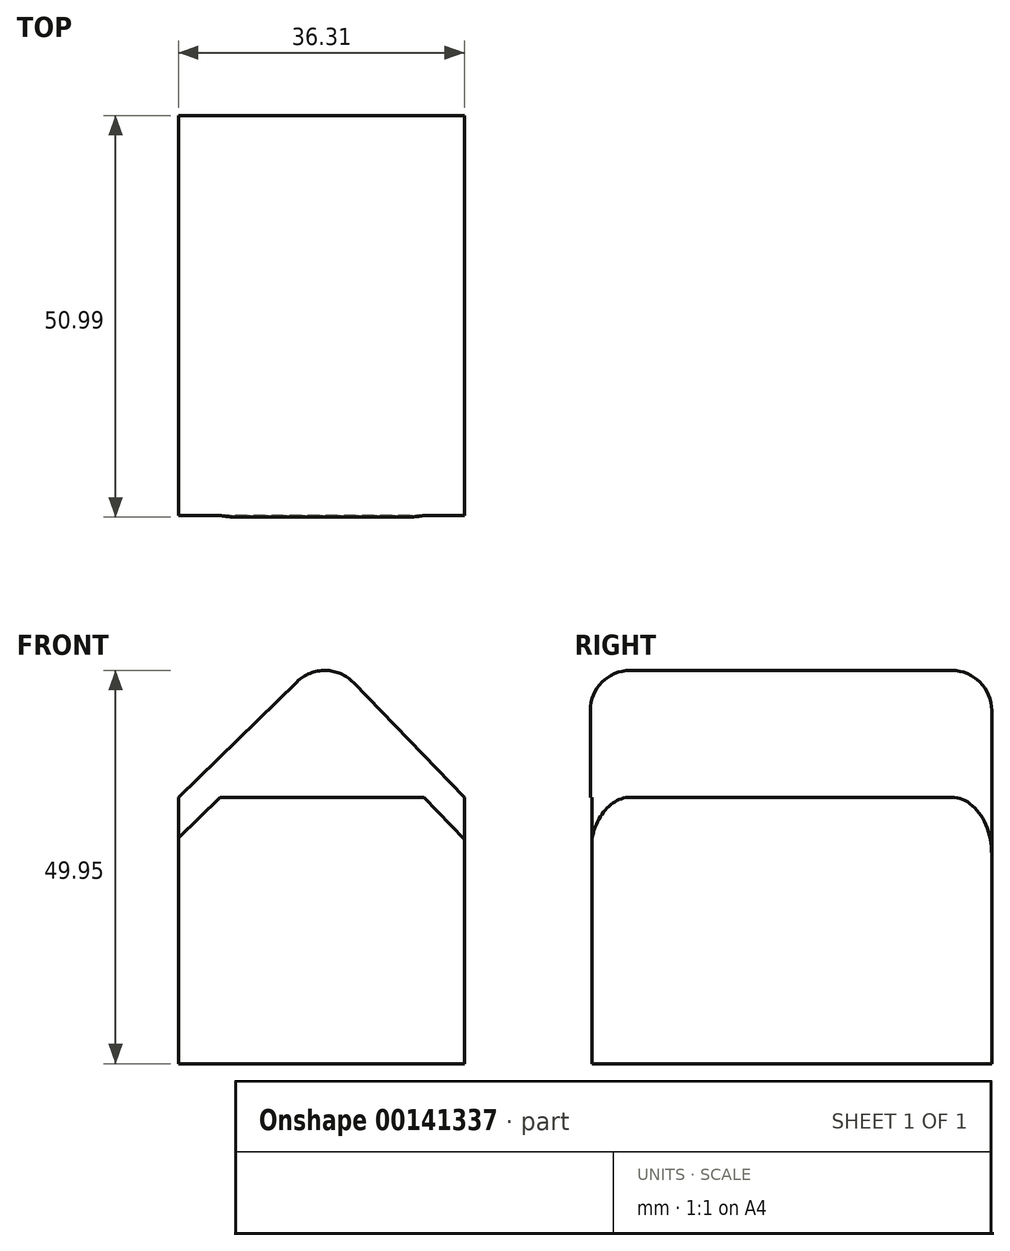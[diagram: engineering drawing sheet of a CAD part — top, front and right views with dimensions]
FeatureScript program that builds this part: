
annotation { "Feature Type Name" : "Feature", "Feature Type Description" : "" }
export const myFeature = defineFeature(function(context is Context, id is Id, definition is map)
    precondition{}
    {
        {
            var Q0;
            Q0=qCreatedBy(makeId("Front.planeOp"),FACE);
            var sketch = newSketch(context, id + "F0", { "sketchPlane" : qUnion([Q0])});
            skLineSegment(sketch, "E0", {"start": v(0, 0) * mm, "end": v(-36.3, 0) * mm});
            skLineSegment(sketch, "E1", {"start": v(-36.3, 0) * mm, "end": v(-36.3, 33.84) * mm});
            skLineSegment(sketch, "E2", {"start": v(-36.3, 33.84) * mm, "end": v(0, 33.84) * mm});
            skLineSegment(sketch, "E3", {"start": v(0, 33.84) * mm, "end": v(0, 0) * mm});
            skSolve(sketch);
        }
        {
            var Q0;
            Q0 = qSketchRegion(id + "F0", true);
            extrude(context, id + "F1", {"entities" : qUnion([Q0]), "endBound" : BoundingType.SYMMETRIC, "depth" : 50.8 * mm});
        }
        {
            var Q0;
            Q0=makeQuery(id+"F1.opExtrude","CAP_FACE",FACE,{"disambiguationData":[OSD([sQuery(id+"F0.wireOp",EDGE,"E0"),sQuery(id+"F0.wireOp",EDGE,"E1"),sQuery(id+"F0.wireOp",EDGE,"E2"),sQuery(id+"F0.wireOp",EDGE,"E3")])],"isStart":false});
            var sketch = newSketch(context, id + "F2", { "sketchPlane" : qUnion([Q0])});
            skLineSegment(sketch, "E4", {"start": v(-18.15, 0) * mm, "end": v(-18.15, 9.47) * mm});
            skLineSegment(sketch, "E5", {"start": v(-18.15, 9.47) * mm, "end": v(-14.04, 9.47) * mm});
            skLineSegment(sketch, "E6", {"start": v(-14.04, 9.3) * mm, "end": v(-14.04, 0) * mm});
            skLineSegment(sketch, "E7", {"start": v(-31.06, 22.8) * mm, "end": v(-27.02, 22.8) * mm});
            skLineSegment(sketch, "E8", {"start": v(-27.02, 22.8) * mm, "end": v(-27.02, 18.95) * mm});
            skLineSegment(sketch, "E9", {"start": v(-26.85, 18.95) * mm, "end": v(-31.23, 18.95) * mm});
            skLineSegment(sketch, "E10", {"start": v(-31.23, 19.13) * mm, "end": v(-31.06, 22.8) * mm});
            skLineSegment(sketch, "E11", {"start": v(-7.54, 22.46) * mm, "end": v(-4.21, 22.46) * mm});
            skLineSegment(sketch, "E12", {"start": v(-4.21, 22.8) * mm, "end": v(-4.21, 16.84) * mm});
            skLineSegment(sketch, "E13", {"start": v(-4.56, 16.84) * mm, "end": v(-9.3, 16.84) * mm});
            skLineSegment(sketch, "E14", {"start": v(-9.3, 17.55) * mm, "end": v(-9.3, 21.4) * mm});
            skLineSegment(sketch, "E15", {"start": v(-9.3, 21.4) * mm, "end": v(-9.3, 22.46) * mm});
            skLineSegment(sketch, "E16", {"start": v(-9.3, 22.46) * mm, "end": v(-9.3, 21.4) * mm});
            skLineSegment(sketch, "E17", {"start": v(-7.54, 22.46) * mm, "end": v(-9.3, 22.46) * mm});
            skSolve(sketch);
        }
        {
            var Q0;
            Q0=makeQuery(id+"F1.opExtrude","CAP_FACE",FACE,{"disambiguationData":[OSD([sQuery(id+"F0.wireOp",EDGE,"E0"),sQuery(id+"F0.wireOp",EDGE,"E1"),sQuery(id+"F0.wireOp",EDGE,"E2"),sQuery(id+"F0.wireOp",EDGE,"E3")])],"isStart":true});
            var sketch = newSketch(context, id + "F3", { "sketchPlane" : qUnion([Q0])});
            skLineSegment(sketch, "E18", {"start": v(17.62, 52.08) * mm, "end": v(0, 33.84) * mm});
            skLineSegment(sketch, "E19", {"start": v(17.62, 52.08) * mm, "end": v(36.3, 33.84) * mm});
            skSolve(sketch);
        }
        {
            var Q0;
            Q0=qCreatedBy(makeId("Top.planeOp"),FACE);
            var sketch = newSketch(context, id + "F4", { "sketchPlane" : qUnion([Q0])});
            skSolve(sketch);
        }
        {
            var Q0;
            Q0 = qSketchRegion(id + "F4", true);
            var Q1;
            Q1 = qSketchRegion(id + "F2", true);
            var Q2;
            Q2 = qSketchRegion(id + "F3", true);
            var Q3;
            Q3=makeQuery(id+"F3.imprint","IMPRINT",FACE,{"disambiguationData":[TD([[makeQuery(id+"F3.imprint","IMPRINT",EDGE,{"derivedFrom":sQuery(id+"F3.wireOp",EDGE,"E18")}),1.0]])]});
            extrude(context, id + "F5", {"entities" : qUnion([Q0, Q1, Q2, Q3]), "operationType" : NewBodyOperationType.ADD, "oppositeDirection" : true, "depth" : 51 * mm});
        }
        {
            var Q0;
            Q0=makeQuery(id+"F5.opExtrude","CAP_EDGE",EDGE,{"disambiguationData":[OSD([sQuery(id+"F3.wireOp",EDGE,"E19")])],"isStart":false});
            fillet(context, id + "F6", {"entities" : qUnion([Q0]), "radius" : 5.08 * mm, "tangentPropagation" : true, "allowEdgeOverflow" : false});
        }
        {
            var Q0;
            Q0=makeQuery(id+"F5.opExtrude","CAP_EDGE",EDGE,{"disambiguationData":[OSD([sQuery(id+"F3.wireOp",EDGE,"E18")])],"isStart":false});
            var Q1;
            Q1=makeQuery(id+"F5.opExtrude","CAP_EDGE",EDGE,{"disambiguationData":[OSD([sQuery(id+"F3.wireOp",EDGE,"E19")])],"isStart":true});
            var Q2;
            Q2=makeQuery(id+"F5.opExtrude","CAP_EDGE",EDGE,{"disambiguationData":[OSD([sQuery(id+"F3.wireOp",EDGE,"E18")])],"isStart":true});
            fillet(context, id + "F7", {"entities" : qUnion([Q0, Q1, Q2]), "radius" : 5.08 * mm, "tangentPropagation" : true, "allowEdgeOverflow" : false});
        }
    });
